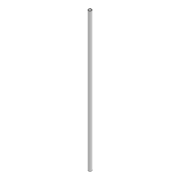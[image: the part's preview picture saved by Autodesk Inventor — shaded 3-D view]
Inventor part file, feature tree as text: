
AUTODESK INVENTOR PART (.ipt)
format: ipt  version: 2022 (Build 260153000, 153)  size: 77,312 bytes
history: native  units: mm
features: extrude x1, sketch x1
ambient origin geometry x8: Origin, YZ Plane, XZ Plane, XY Plane, X Axis, Y Axis, Z Axis, Center Point
bodies: Solid1 (feature_tree)
feature tree (2):
  extrude  "Extrusion1"  Depth=10.0mm
  sketch  "Sketch1"  dims[d0=12.0mm d1=10.0mm d2=500.0mm d3=0.0mm]
